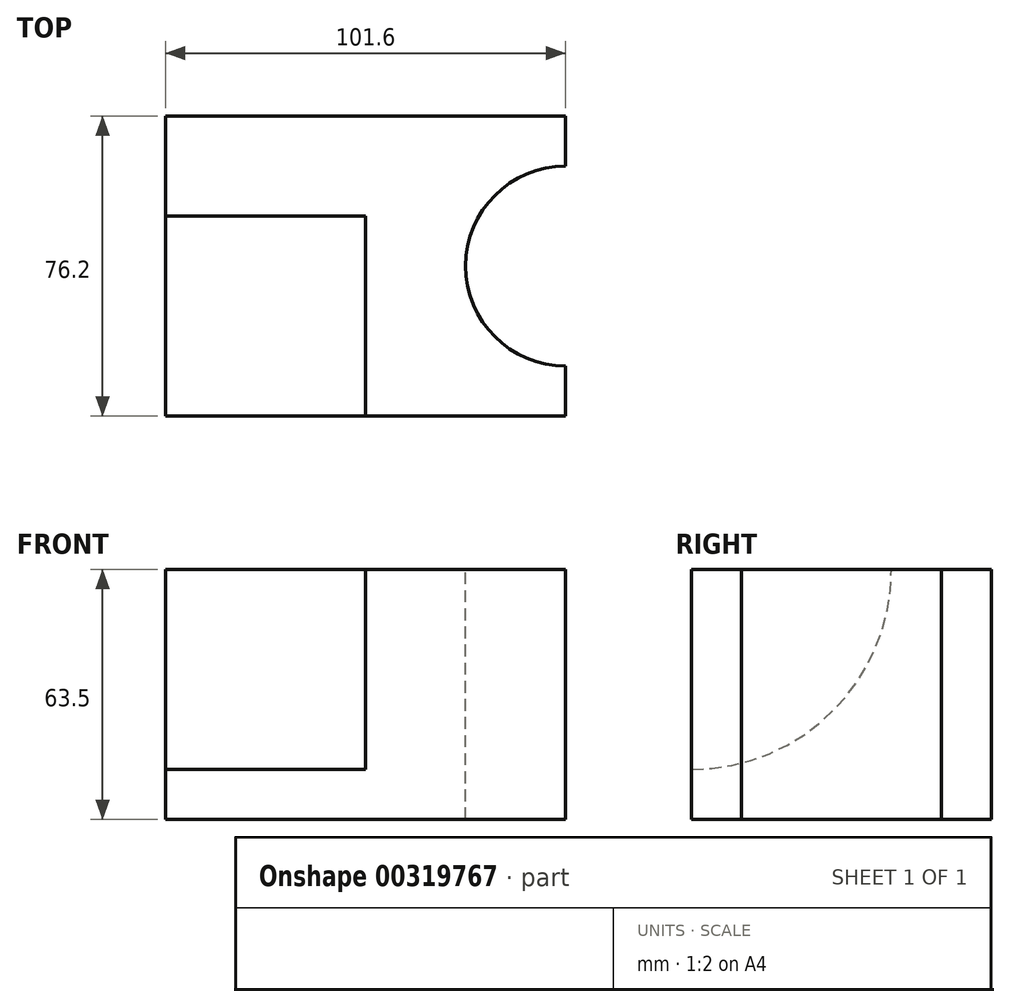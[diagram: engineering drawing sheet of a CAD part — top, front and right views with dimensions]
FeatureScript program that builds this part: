
annotation { "Feature Type Name" : "Feature", "Feature Type Description" : "" }
export const myFeature = defineFeature(function(context is Context, id is Id, definition is map)
    precondition{}
    {
        {
            var Q0;
            Q0=qCreatedBy(makeId("Front.planeOp"),FACE);
            var sketch = newSketch(context, id + "F0", { "sketchPlane" : qUnion([Q0])});
            skLineSegment(sketch, "E0", {"start": v(-48.14, -43.8) * mm, "end": v(53.46, -43.8) * mm});
            skLineSegment(sketch, "E1", {"start": v(53.46, -43.8) * mm, "end": v(53.46, 19.7) * mm});
            skLineSegment(sketch, "E2", {"start": v(53.46, 19.7) * mm, "end": v(-48.14, 19.7) * mm});
            skLineSegment(sketch, "E3", {"start": v(-48.14, 19.7) * mm, "end": v(-48.14, -43.8) * mm});
            skSolve(sketch);
        }
        {
            var Q0;
            Q0=makeQuery(id+"F0.imprint","IMPRINT",FACE,{"disambiguationData":[TD([[makeQuery(id+"F0.imprint","IMPRINT",EDGE,{"derivedFrom":sQuery(id+"F0.wireOp",EDGE,"E0")}),1.0]])]});
            extrude(context, id + "F1", {"entities" : qUnion([Q0]), "oppositeDirection" : true, "depth" : 76.2 * mm});
        }
        {
            var Q0;
            Q0=makeQuery(id+"F1.opExtrude","SWEPT_FACE",FACE,{"disambiguationData":[OSD([sQuery(id+"F0.wireOp",EDGE,"E2")])]});
            var sketch = newSketch(context, id + "F2", { "sketchPlane" : qUnion([Q0])});
            skArc(sketch, "E4", {"start": v(53.46, 63.5) * mm, "mid": v(28.06, 38.1) * mm, "end": v(53.46, 12.7) * mm});
            skSolve(sketch);
        }
        {
            var Q0;
            {var subQ0=sQuery(id+"F2.wireOp",EDGE,"E4");Q0=makeQuery(id+"F2.imprint","IMPRINT",FACE,{"disambiguationData":[TD([[makeQuery(id+"F2.imprint","IMPRINT",EDGE,{"derivedFrom":subQ0}),1.0]])]});}
            extrude(context, id + "F3", {"entities" : qUnion([Q0]), "operationType" : NewBodyOperationType.REMOVE, "oppositeDirection" : true, "depth" : 63.5 * mm});
        }
        {
            var Q0;
            Q0=makeQuery(id+"F1.opExtrude","SWEPT_FACE",FACE,{"disambiguationData":[OSD([sQuery(id+"F0.wireOp",EDGE,"E3")])]});
            var sketch = newSketch(context, id + "F4", { "sketchPlane" : qUnion([Q0])});
            skArc(sketch, "E5", {"start": v(-50.8, 19.7) * mm, "mid": v(-35.92, -16.22) * mm, "end": v(0, -31.1) * mm});
            skLineSegment(sketch, "E6", {"start": v(-50.8, 19.7) * mm, "end": v(0, 19.7) * mm});
            skLineSegment(sketch, "E7", {"start": v(0, -31.1) * mm, "end": v(0, 19.7) * mm});
            skSolve(sketch);
        }
        {
            var Q0;
            Q0=makeQuery(id+"F4.imprint","IMPRINT",FACE,{"disambiguationData":[TD([[makeQuery(id+"F4.imprint","IMPRINT",EDGE,{"derivedFrom":sQuery(id+"F4.wireOp",EDGE,"E5")}),1.0]])]});
            extrude(context, id + "F5", {"entities" : qUnion([Q0]), "operationType" : NewBodyOperationType.REMOVE, "oppositeDirection" : true, "depth" : 50.8 * mm});
        }
    });
